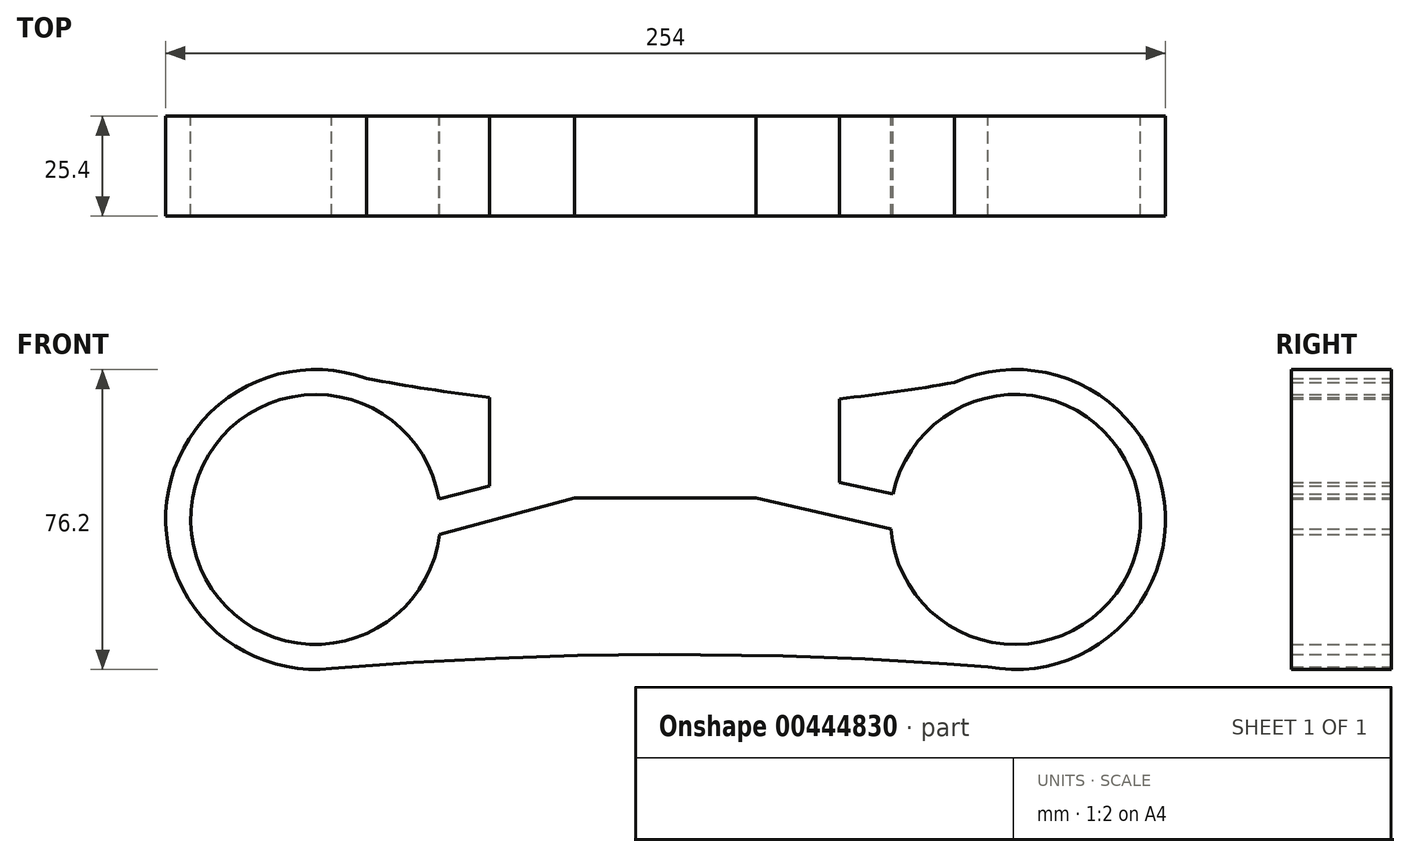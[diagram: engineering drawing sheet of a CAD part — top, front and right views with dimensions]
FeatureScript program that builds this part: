
annotation { "Feature Type Name" : "Feature", "Feature Type Description" : "" }
export const myFeature = defineFeature(function(context is Context, id is Id, definition is map)
    precondition{}
    {
        {
            var Q0;
            Q0=qCreatedBy(makeId("Front.planeOp"),FACE);
            var sketch = newSketch(context, id + "F0", { "sketchPlane" : qUnion([Q0])});
            skArc(sketch, "E0", {"start": v(-53.46, 7.84) * mm, "mid": v(-128.97, -1.35) * mm, "end": v(-52.9, -1.04) * mm});
            skArc(sketch, "E1", {"start": v(48.76, 0.13) * mm, "mid": v(124.8, -2.44) * mm, "end": v(49.56, 8.84) * mm});
            skArc(sketch, "E2", {"start": v(-88.68, 39.07) * mm, "mid": v(-67.81, 35.03) * mm, "end": v(-46.76, 32.08) * mm});
            skArc(sketch, "E3", {"start": v(87.75, -37.05) * mm, "mid": v(-0.46, -33.29) * mm, "end": v(-88.68, -37) * mm});
            skArc(sketch, "E4", {"start": v(-59.63, 6.24) * mm, "mid": v(-122.7, 0.34) * mm, "end": v(-59.43, -2.8) * mm});
            skArc(sketch, "E5", {"start": v(55.19, -1.33) * mm, "mid": v(118.53, -1.02) * mm, "end": v(55.76, 7.46) * mm});
            skLineSegment(sketch, "E6", {"start": v(-25.14, 6.46) * mm, "end": v(20.9, 6.46) * mm});
            skLineSegment(sketch, "E7", {"start": v(-46.76, 9.59) * mm, "end": v(-59.63, 6.24) * mm});
            skLineSegment(sketch, "E8", {"start": v(-59.43, -2.8) * mm, "end": v(-25.14, 6.46) * mm});
            skLineSegment(sketch, "E9", {"start": v(42.14, 10.5) * mm, "end": v(55.76, 7.46) * mm});
            skLineSegment(sketch, "E10", {"start": v(55.19, -1.33) * mm, "end": v(20.9, 6.46) * mm});
            skArc(sketch, "E11.trimOffspring", {"start": v(42.14, 31.7) * mm, "mid": v(65.05, 34.77) * mm, "end": v(87.75, 39.12) * mm});
            skPoint(sketch, "E12.orphan", {"position": v(-64.63, 4.94) * mm});
            skPoint(sketch, "E13.orphan", {"position": v(-62.4, -3.6) * mm});
            skPoint(sketch, "E14.orphan", {"position": v(67.1, 4.94) * mm});
            skPoint(sketch, "E15.orphan", {"position": v(65.2, -3.6) * mm});
            skLineSegment(sketch, "E16.left", {"start": v(-46.76, 32.08) * mm, "end": v(-46.76, 9.59) * mm});
            skLineSegment(sketch, "E16.right", {"start": v(42.14, 31.7) * mm, "end": v(42.14, 10.5) * mm});
            skPoint(sketch, "E17.orphan", {"position": v(-25.14, 15.2) * mm});
            skPoint(sketch, "E18.orphan", {"position": v(20.9, 15.2) * mm});
            skSolve(sketch);
        }
        {
            var Q0;
            Q0 = qSketchRegion(id + "F0", true);
            extrude(context, id + "F1", {"entities" : qUnion([Q0]), "depth" : 25.4 * mm});
        }
    });
